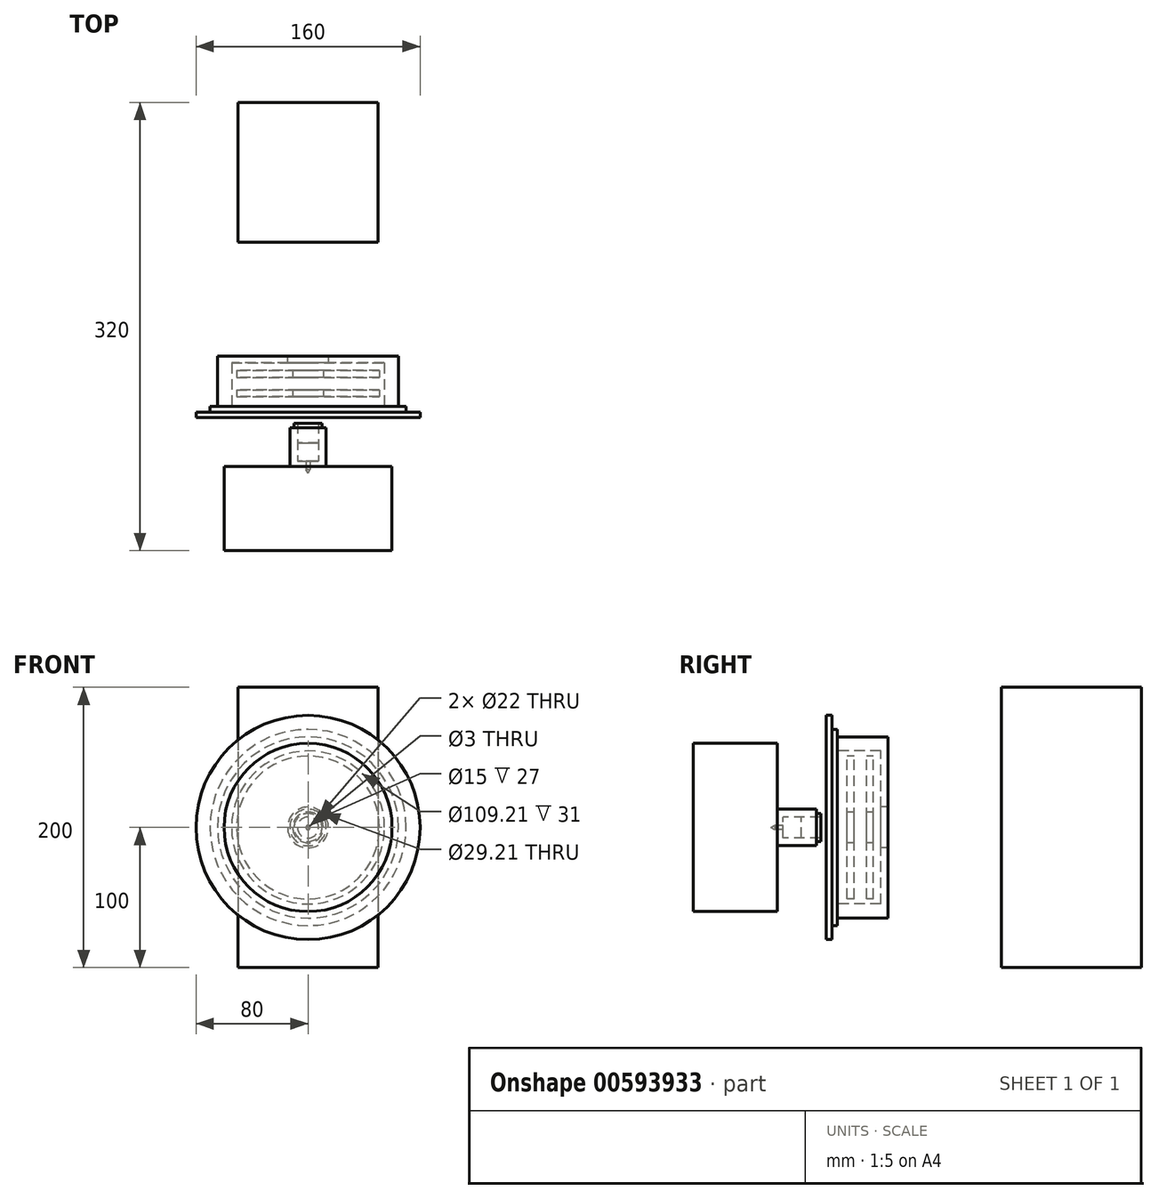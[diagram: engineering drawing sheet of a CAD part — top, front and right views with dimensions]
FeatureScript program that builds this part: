
annotation { "Feature Type Name" : "Feature", "Feature Type Description" : "" }
export const myFeature = defineFeature(function(context is Context, id is Id, definition is map)
    precondition{}
    {
        {
            var Q0;
            Q0=qCreatedBy(makeId("Right.planeOp"),FACE);
            var sketch = newSketch(context, id + "F0", { "sketchPlane" : qUnion([Q0])});
            skLineSegment(sketch, "E0.bottom", {"start": v(117, 100) * mm, "end": v(217, 100) * mm});
            skLineSegment(sketch, "E0.top", {"start": v(117, -100) * mm, "end": v(217, -100) * mm});
            skLineSegment(sketch, "E0.left", {"start": v(117, 100) * mm, "end": v(117, -100) * mm});
            skLineSegment(sketch, "E0.right", {"start": v(217, 100) * mm, "end": v(217, -100) * mm});
            skLineSegment(sketch, "E1.right", {"start": v(0, 70) * mm, "end": v(0, -40.74) * mm});
            skLineSegment(sketch, "E2.bottom", {"start": v(-39, 7.5) * mm, "end": v(-12, 7.5) * mm});
            skLineSegment(sketch, "E2.left", {"start": v(-39, 7.5) * mm, "end": v(-39, 1.5) * mm});
            skLineSegment(sketch, "E2.right", {"start": v(-12, 7.5) * mm, "end": v(-12, 0) * mm});
            skLineSegment(sketch, "E3.bottom", {"start": v(0, 70) * mm, "end": v(-4, 70) * mm});
            skLineSegment(sketch, "E4.bottom", {"start": v(-8, 80) * mm, "end": v(-4, 80) * mm});
            skLineSegment(sketch, "E4.left", {"start": v(-8, 80) * mm, "end": v(-8, 0) * mm});
            skLineSegment(sketch, "E4.right", {"start": v(-4, 80) * mm, "end": v(-4, 70) * mm});
            skLineSegment(sketch, "E5.bottom", {"start": v(-12, 7.5) * mm, "end": v(-26, 7.5) * mm});
            skLineSegment(sketch, "E5.top", {"start": v(-12, 10) * mm, "end": v(-15.18, 10) * mm});
            skLineSegment(sketch, "E5.left", {"start": v(-12, 7.5) * mm, "end": v(-12, 10) * mm});
            skLineSegment(sketch, "E6.bottom", {"start": v(-15.18, 13) * mm, "end": v(-57, 13) * mm});
            skLineSegment(sketch, "E6.left", {"start": v(-15.18, 13) * mm, "end": v(-15.18, 10) * mm});
            skLineSegment(sketch, "E7", {"start": v(-39, 1.5) * mm, "end": v(-45, 1.5) * mm});
            skLineSegment(sketch, "E8", {"start": v(-45, 1.5) * mm, "end": v(-47.6, 0) * mm});
            skLineSegment(sketch, "E9", {"start": v(-26, 7.5) * mm, "end": v(-26, 0) * mm});
            skLineSegment(sketch, "E10.bottom", {"start": v(-43, 60) * mm, "end": v(-103, 60) * mm});
            skLineSegment(sketch, "E10.left", {"start": v(-43, 60) * mm, "end": v(-43, 13) * mm});
            skLineSegment(sketch, "E10.right", {"start": v(-103, 60) * mm, "end": v(-103, 0) * mm});
            skLineSegment(sketch, "E11", {"start": v(-57, 13) * mm, "end": v(-57, 0) * mm});
            skLineSegment(sketch, "E12", {"start": v(-103, 0) * mm, "end": v(125.46, 0) * mm});
            skPoint(sketch, "E13.right.start.orphan", {"position": v(-12, 0) * mm});
            skPoint(sketch, "E14", {"position": v(-39, 1.5) * mm});
            skPoint(sketch, "E15", {"position": v(-45, 1.5) * mm});
            skPoint(sketch, "E16", {"position": v(-47.6, 0) * mm});
            skLineSegment(sketch, "E17.bottom", {"start": v(0, 64.6) * mm, "end": v(36, 64.6) * mm});
            skLineSegment(sketch, "E17.top", {"start": v(0, 54.6) * mm, "end": v(31, 54.6) * mm});
            skLineSegment(sketch, "E17.left", {"start": v(0, 64.6) * mm, "end": v(0, 54.6) * mm});
            skLineSegment(sketch, "E17.right", {"start": v(36, 64.6) * mm, "end": v(36, 54.6) * mm});
            skLineSegment(sketch, "E18.bottom", {"start": v(36, 14.6) * mm, "end": v(31, 14.6) * mm});
            skLineSegment(sketch, "E18.left", {"start": v(36, 14.6) * mm, "end": v(36, 54.6) * mm});
            skLineSegment(sketch, "E18.right", {"start": v(31, 14.6) * mm, "end": v(31, 54.6) * mm});
            skLineSegment(sketch, "E19.bottom", {"start": v(6.87, 51) * mm, "end": v(11.87, 51) * mm});
            skLineSegment(sketch, "E19.top", {"start": v(6.87, 11) * mm, "end": v(11.87, 11) * mm});
            skLineSegment(sketch, "E19.left", {"start": v(6.87, 51) * mm, "end": v(6.87, 11) * mm});
            skLineSegment(sketch, "E19.right", {"start": v(11.87, 51) * mm, "end": v(11.87, 11) * mm});
            skLineSegment(sketch, "E20.bottom", {"start": v(20.7, 51) * mm, "end": v(25.7, 51) * mm});
            skLineSegment(sketch, "E20.top", {"start": v(20.7, 11) * mm, "end": v(25.7, 11) * mm});
            skLineSegment(sketch, "E20.left", {"start": v(25.7, 51) * mm, "end": v(25.7, 11) * mm});
            skLineSegment(sketch, "E20.right", {"start": v(20.7, 51) * mm, "end": v(20.7, 11) * mm});
            skSolve(sketch);
        }
        {
            var Q0;
            {var subQ3=sQuery(id+"F0.wireOp",EDGE,"E0.bottom");Q0=makeQuery(id+"F0.imprint","IMPRINT",FACE,{"disambiguationData":[TD([[makeQuery(id+"F0.imprint","IMPRINT",EDGE,{"derivedFrom":subQ3}),-1.0]])]});}
            extrude(context, id + "F1", {"entities" : qUnion([Q0]), "endBound" : BoundingType.SYMMETRIC, "depth" : 100 * mm, "offsetDistance" : 25 * mm});
        }
        {
            var Q0;
            Q0=makeQuery(id+"F0.imprint","IMPRINT",FACE,{"disambiguationData":[TD([[makeQuery(id+"F0.imprint","IMPRINT",EDGE,{"derivedFrom":sQuery(id+"F0.wireOp",EDGE,"E17.bottom")}),-1.0]])]});
            var Q1;
            Q1=sQuery(id+"F0.wireOp",EDGE,"E12");
            revolve(context, id + "F2", {"operationType" : NewBodyOperationType.ADD, "entities" : qUnion([Q0]), "axis" : qUnion([Q1]), "revolveType" : RevolveType.FULL});
        }
        {
            var Q0;
            {var subQ0=sQuery(id+"F0.wireOp",EDGE,"E3.bottom");Q0=makeQuery(id+"F0.imprint","IMPRINT",FACE,{"disambiguationData":[TD([[makeQuery(id+"F0.imprint","IMPRINT",EDGE,{"derivedFrom":subQ0}),1.0]])]});}
            var Q1;
            Q1=sQuery(id+"F0.wireOp",EDGE,"E12");
            revolve(context, id + "F3", {"entities" : qUnion([Q0]), "axis" : qUnion([Q1]), "revolveType" : RevolveType.FULL});
        }
        {
            var Q0;
            {var subQ0=sQuery(id+"F0.wireOp",EDGE,"E2.right");Q0=makeQuery(id+"F0.imprint","IMPRINT",FACE,{"disambiguationData":[TD([[makeQuery(id+"F0.imprint","IMPRINT",EDGE,{"derivedFrom":subQ0}),-1.0]])]});}
            var Q1;
            Q1=sQuery(id+"F0.wireOp",EDGE,"E12");
            revolve(context, id + "F4", {"entities" : qUnion([Q0]), "axis" : qUnion([Q1]), "revolveType" : RevolveType.FULL});
        }
        {
            var Q0;
            Q0=makeQuery(id+"F0.imprint","IMPRINT",FACE,{"disambiguationData":[TD([[makeQuery(id+"F0.imprint","IMPRINT",EDGE,{"derivedFrom":sQuery(id+"F0.wireOp",EDGE,"E2.bottom")}),1.0]])]});
            var Q1;
            Q1=sQuery(id+"F0.wireOp",EDGE,"E12");
            revolve(context, id + "F5", {"entities" : qUnion([Q0]), "axis" : qUnion([Q1]), "revolveType" : RevolveType.FULL});
        }
        {
            var Q0;
            Q0=makeQuery(id+"F0.imprint","IMPRINT",FACE,{"disambiguationData":[TD([[makeQuery(id+"F0.imprint","IMPRINT",EDGE,{"derivedFrom":sQuery(id+"F0.wireOp",EDGE,"E10.bottom")}),1.0]])]});
            var Q1;
            Q1=sQuery(id+"F0.wireOp",EDGE,"E12");
            revolve(context, id + "F6", {"operationType" : NewBodyOperationType.ADD, "entities" : qUnion([Q0]), "axis" : qUnion([Q1]), "revolveType" : RevolveType.FULL});
        }
        {
            var Q0;
            Q0=makeQuery(id+"F0.imprint","IMPRINT",FACE,{"disambiguationData":[TD([[makeQuery(id+"F0.imprint","IMPRINT",EDGE,{"derivedFrom":sQuery(id+"F0.wireOp",EDGE,"E19.bottom")}),-1.0]])]});
            var Q1;
            Q1=sQuery(id+"F0.wireOp",EDGE,"E12");
            revolve(context, id + "F7", {"entities" : qUnion([Q0]), "axis" : qUnion([Q1]), "revolveType" : RevolveType.FULL});
        }
        {
            var Q0;
            Q0=makeQuery(id+"F0.imprint","IMPRINT",FACE,{"disambiguationData":[TD([[makeQuery(id+"F0.imprint","IMPRINT",EDGE,{"derivedFrom":sQuery(id+"F0.wireOp",EDGE,"E20.bottom")}),-1.0]])]});
            var Q1;
            Q1=sQuery(id+"F0.wireOp",EDGE,"E12");
            revolve(context, id + "F8", {"entities" : qUnion([Q0]), "axis" : qUnion([Q1]), "revolveType" : RevolveType.FULL});
        }
    });
